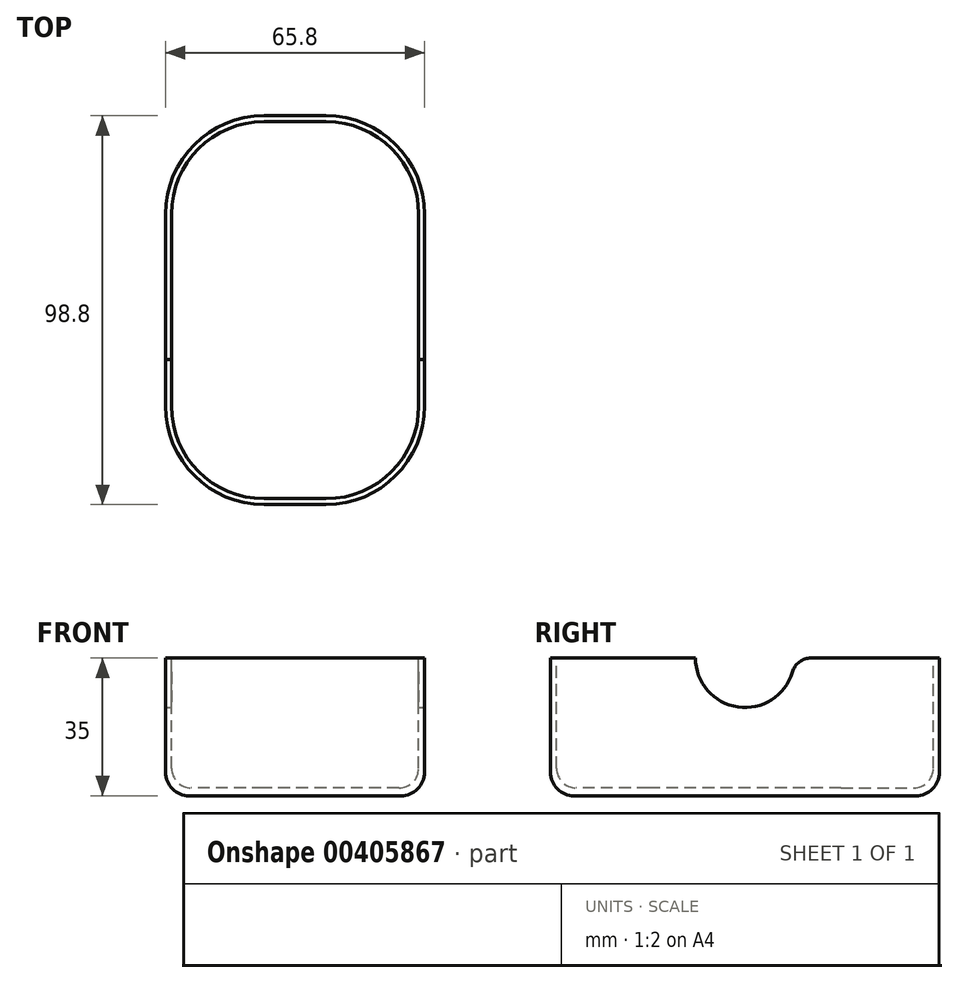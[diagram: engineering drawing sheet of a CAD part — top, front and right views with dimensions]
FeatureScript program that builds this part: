
annotation { "Feature Type Name" : "Feature", "Feature Type Description" : "" }
export const myFeature = defineFeature(function(context is Context, id is Id, definition is map)
    precondition{}
    {
        {
            var Q0;
            Q0=qCreatedBy(makeId("Top.planeOp"),FACE);
            var sketch = newSketch(context, id + "F0", { "sketchPlane" : qUnion([Q0])});
            skLineSegment(sketch, "E0.bottom", {"start": v(32.9, 49.4) * mm, "end": v(-32.9, 49.4) * mm});
            skLineSegment(sketch, "E0.top", {"start": v(32.9, -49.4) * mm, "end": v(-32.9, -49.4) * mm});
            skLineSegment(sketch, "E0.left", {"start": v(32.9, 49.4) * mm, "end": v(32.9, -49.4) * mm});
            skLineSegment(sketch, "E0.right", {"start": v(-32.9, 49.4) * mm, "end": v(-32.9, -49.4) * mm});
            skPoint(sketch, "E0.middle", {"position": v(0, 0) * mm});
            skSolve(sketch);
        }
        {
            var Q0;
            Q0=makeQuery(id+"F0.imprint","IMPRINT",FACE,{"disambiguationData":[TD([[makeQuery(id+"F0.imprint","IMPRINT",EDGE,{"derivedFrom":sQuery(id+"F0.wireOp",EDGE,"E0.bottom")}),1.0]])]});
            extrude(context, id + "F1", {"entities" : qUnion([Q0]), "depth" : 35 * mm});
        }
        {
            var Q0;
            Q0=makeQuery(id+"F1.opExtrude","SWEPT_EDGE",EDGE,{"disambiguationData":[OSD([sQuery(id+"F0.wireOp",EDGE,"E0.bottom"),sQuery(id+"F0.wireOp",EDGE,"E0.left")])]});
            var Q1;
            Q1=makeQuery(id+"F1.opExtrude","SWEPT_EDGE",EDGE,{"disambiguationData":[OSD([sQuery(id+"F0.wireOp",EDGE,"E0.bottom"),sQuery(id+"F0.wireOp",EDGE,"E0.right")])]});
            var Q2;
            Q2=makeQuery(id+"F1.opExtrude","SWEPT_EDGE",EDGE,{"disambiguationData":[OSD([sQuery(id+"F0.wireOp",EDGE,"E0.top"),sQuery(id+"F0.wireOp",EDGE,"E0.left")])]});
            var Q3;
            Q3=makeQuery(id+"F1.opExtrude","SWEPT_EDGE",EDGE,{"disambiguationData":[OSD([sQuery(id+"F0.wireOp",EDGE,"E0.top"),sQuery(id+"F0.wireOp",EDGE,"E0.right")])]});
            fillet(context, id + "F2", {"entities" : qUnion([Q0, Q1, Q2, Q3]), "radius" : 25 * mm, "tangentPropagation" : true, "allowEdgeOverflow" : false});
        }
        {
            var Q0;
            Q0=makeQuery(id+"F1.opExtrude","CAP_FACE",FACE,{"disambiguationData":[OSD([sQuery(id+"F0.wireOp",EDGE,"E0.bottom"),sQuery(id+"F0.wireOp",EDGE,"E0.top"),sQuery(id+"F0.wireOp",EDGE,"E0.left"),sQuery(id+"F0.wireOp",EDGE,"E0.right")])],"isStart":false});
            var sketch = newSketch(context, id + "F3", { "sketchPlane" : qUnion([Q0])});
            skArc(sketch, "E1.0", {"start": v(31.4, 24.4) * mm, "mid": v(24.52, 41.02) * mm, "end": v(7.9, 47.9) * mm});
            skLineSegment(sketch, "E1.1", {"start": v(7.9, 47.9) * mm, "end": v(-7.9, 47.9) * mm});
            skLineSegment(sketch, "E1.2", {"start": v(31.4, 24.4) * mm, "end": v(31.4, -24.4) * mm});
            skArc(sketch, "E1.3", {"start": v(-7.9, 47.9) * mm, "mid": v(-24.52, 41.02) * mm, "end": v(-31.4, 24.4) * mm});
            skArc(sketch, "E1.4", {"start": v(7.9, -47.9) * mm, "mid": v(24.52, -41.02) * mm, "end": v(31.4, -24.4) * mm});
            skLineSegment(sketch, "E1.5", {"start": v(7.9, -47.9) * mm, "end": v(-7.9, -47.9) * mm});
            skArc(sketch, "E1.6", {"start": v(-31.4, -24.4) * mm, "mid": v(-24.52, -41.02) * mm, "end": v(-7.9, -47.9) * mm});
            skLineSegment(sketch, "E1.7", {"start": v(-31.4, 24.4) * mm, "end": v(-31.4, -24.4) * mm});
            skSolve(sketch);
        }
        {
            var Q0;
            Q0=makeQuery(id+"F3.imprint","IMPRINT",FACE,{"disambiguationData":[TD([[makeQuery(id+"F3.imprint","IMPRINT",EDGE,{"derivedFrom":sQuery(id+"F3.wireOp",EDGE,"E1.0")}),1.0]])]});
            extrude(context, id + "F4", {"entities" : qUnion([Q0]), "operationType" : NewBodyOperationType.REMOVE, "oppositeDirection" : true, "depth" : 33 * mm});
        }
        {
            var Q0;
            Q0=makeQuery(id+"F1.opExtrude","SWEPT_FACE",FACE,{"disambiguationData":[OSD([sQuery(id+"F0.wireOp",EDGE,"E0.left")])]});
            var sketch = newSketch(context, id + "F5", { "sketchPlane" : qUnion([Q0])});
            skCircle(sketch, "E2", {"center": v(0, 35) * mm, "radius": 12.57 * mm});
            skSolve(sketch);
        }
        {
            var Q0;
            {var subQ0=sQuery(id+"F5.wireOp",EDGE,"E2");var subQ1=makeQuery(id+"F1.opExtrude","CAP_EDGE",EDGE,{"disambiguationData":[OSD([sQuery(id+"F0.wireOp",EDGE,"E0.left")])],"isStart":false});var subQ2=makeQuery(id+"F5.imprint","INTERSECT",VERTEX,{"disambiguationData":[OD(0.0)],"derivedFrom":[subQ1,subQ0]});Q0=makeQuery(id+"F5.imprint","IMPRINT",FACE,{"disambiguationData":[TD([[makeQuery(id+"F5.imprint","IMPRINT",EDGE,{"disambiguationData":[TD([[subQ2,1.0]])],"derivedFrom":subQ0}),1.0]])]});}
            var Q1;
            Q1=sQuery(id+"F5.wireOp",EDGE,"E2");
            extrude(context, id + "F6", {"entities" : qUnion([Q0]), "operationType" : NewBodyOperationType.REMOVE, "surfaceEntities" : qUnion([Q1]), "endBound" : BoundingType.THROUGH_ALL, "oppositeDirection" : true, "depth" : 25 * mm});
        }
        {
            var Q0;
            {var subQ0=sQuery(id+"F0.wireOp",EDGE,"E0.left");var subQ1=sQuery(id+"F5.wireOp",EDGE,"E2");Q0=makeQuery(id+"F6.boolean.opBoolean","COPY",EDGE,{"disambiguationData":[TD([makeQuery(id+"F1.opExtrude","SWEPT_FACE",FACE,{"disambiguationData":[OSD([subQ0])]})])],"derivedFrom":makeQuery(id+"F6.opExtrude","SWEPT_EDGE",EDGE,{"disambiguationData":[OSD([subQ0,subQ1]),TDD([makeQuery(id+"F5.imprint","INTERSECT",VERTEX,{"disambiguationData":[OD(0.0)],"derivedFrom":[makeQuery(id+"F1.opExtrude","CAP_EDGE",EDGE,{"disambiguationData":[OSD([subQ0])],"isStart":false}),subQ1]})])]})});}
            var Q1;
            {var subQ0=sQuery(id+"F0.wireOp",EDGE,"E0.right");var subQ1=sQuery(id+"F0.wireOp",EDGE,"E0.left");var subQ2=sQuery(id+"F5.wireOp",EDGE,"E2");Q1=makeQuery(id+"F6.boolean.opBoolean","COPY",EDGE,{"disambiguationData":[TD([makeQuery(id+"F1.opExtrude","SWEPT_FACE",FACE,{"disambiguationData":[OSD([subQ0])]})])],"derivedFrom":makeQuery(id+"F6.opExtrude","SWEPT_EDGE",EDGE,{"disambiguationData":[OSD([subQ1,subQ2]),TDD([makeQuery(id+"F5.imprint","INTERSECT",VERTEX,{"disambiguationData":[OD(0.0)],"derivedFrom":[makeQuery(id+"F1.opExtrude","CAP_EDGE",EDGE,{"disambiguationData":[OSD([subQ1])],"isStart":false}),subQ2]})])]})});}
            var Q2;
            {var subQ0=sQuery(id+"F0.wireOp",EDGE,"E0.left");var subQ1=sQuery(id+"F5.wireOp",EDGE,"E2");Q2=makeQuery(id+"F6.boolean.opBoolean","COPY",EDGE,{"disambiguationData":[TD([makeQuery(id+"F1.opExtrude","SWEPT_FACE",FACE,{"disambiguationData":[OSD([subQ0])]})])],"derivedFrom":makeQuery(id+"F6.opExtrude","SWEPT_EDGE",EDGE,{"disambiguationData":[OSD([subQ0,subQ1]),TDD([makeQuery(id+"F5.imprint","INTERSECT",VERTEX,{"disambiguationData":[OD(1.0)],"derivedFrom":[makeQuery(id+"F1.opExtrude","CAP_EDGE",EDGE,{"disambiguationData":[OSD([subQ0])],"isStart":false}),subQ1]})])]})});}
            var Q3;
            {var subQ0=sQuery(id+"F0.wireOp",EDGE,"E0.right");var subQ1=sQuery(id+"F0.wireOp",EDGE,"E0.left");var subQ2=sQuery(id+"F5.wireOp",EDGE,"E2");Q3=makeQuery(id+"F6.boolean.opBoolean","COPY",EDGE,{"disambiguationData":[TD([makeQuery(id+"F1.opExtrude","SWEPT_FACE",FACE,{"disambiguationData":[OSD([subQ0])]})])],"derivedFrom":makeQuery(id+"F6.opExtrude","SWEPT_EDGE",EDGE,{"disambiguationData":[OSD([subQ1,subQ2]),TDD([makeQuery(id+"F5.imprint","INTERSECT",VERTEX,{"disambiguationData":[OD(1.0)],"derivedFrom":[makeQuery(id+"F1.opExtrude","CAP_EDGE",EDGE,{"disambiguationData":[OSD([subQ1])],"isStart":false}),subQ2]})])]})});}
            fillet(context, id + "F7", {"entities" : qUnion([Q0, Q1, Q2, Q3]), "radius" : 5 * mm, "tangentPropagation" : true, "allowEdgeOverflow" : false});
        }
        {
            var Q0;
            Q0=makeQuery(id+"F4.boolean.opBoolean","COPY",EDGE,{"derivedFrom":makeQuery(id+"F4.opExtrude","CAP_EDGE",EDGE,{"disambiguationData":[OSD([sQuery(id+"F3.wireOp",EDGE,"E1.3")])],"isStart":false})});
            fillet(context, id + "F8", {"entities" : qUnion([Q0]), "radius" : 5 * mm, "tangentPropagation" : true, "allowEdgeOverflow" : false});
        }
        {
            var Q0;
            {var subQ0=sQuery(id+"F0.wireOp",EDGE,"E0.right");var subQ1=sQuery(id+"F0.wireOp",EDGE,"E0.top");Q0=makeQuery(id+"F2.opFillet","BLEND_EDGE",EDGE,{"blendedFrom":[makeQuery(id+"F1.opExtrude","SWEPT_EDGE",EDGE,{"disambiguationData":[OSD([subQ1,subQ0])]}),makeQuery(id+"F1.opExtrude","CAP_FACE",FACE,{"disambiguationData":[OSD([sQuery(id+"F0.wireOp",EDGE,"E0.bottom"),subQ1,sQuery(id+"F0.wireOp",EDGE,"E0.left"),subQ0])],"isStart":true})],"blendedInto":[makeQuery(id+"F1.opExtrude","CAP_FACE",FACE,{"disambiguationData":[OSD([sQuery(id+"F0.wireOp",EDGE,"E0.bottom"),subQ1,sQuery(id+"F0.wireOp",EDGE,"E0.left"),subQ0])],"isStart":true})]});}
            fillet(context, id + "F9", {"entities" : qUnion([Q0]), "radius" : 6 * mm, "tangentPropagation" : true, "allowEdgeOverflow" : false});
        }
    });
